# Revit family: Kohler Caxton 2211IN-0 Family
name_source: partatom
category: Plumbing Fixtures
revit_build: Autodesk Revit 2018 (Build: 20180329_1100(x64)
units: mm (PartAtom-declared; Revit-internal decimal feet)

## family parameters
Cut with Voids When Loaded = No
Host = Face
OmniClass Number = 23.45.05.14.14
OmniClass Title = Sinks/Lavatories
Part Type = Normal
Room Calculation Point = No
Round Connector Dimension = Use Diameter
Shared = No

## types (1)
- Kohler 2211IN-0
    CW Connection = No
    Default Elevation = 914 mm
    Depth = 192 mm  [stored 0.629921 ft]
    Description = Undercounter basin in white
    HW Connection = No
    Length = 537 mm  [stored 1.76181 ft]
    Manufacturer = KOHLER Co.
    Material1 = Kohler-Vitreous_China-0-White
    Model = Kohler Caxton 2211IN-0
    Type Image = <None>
    URL = https://www.us.kohler.com
    Vent Connection = No
    Waste Connection = Yes
    Width = 439 mm  [stored 1.44029 ft]

note: [stored X ft] marks values corroborated as IEEE doubles in the binary element streams (Revit-internal decimal feet)

## geometry (parser evidence)
native form markers: Sweep x2
no freeform markers — native parametric forms only
